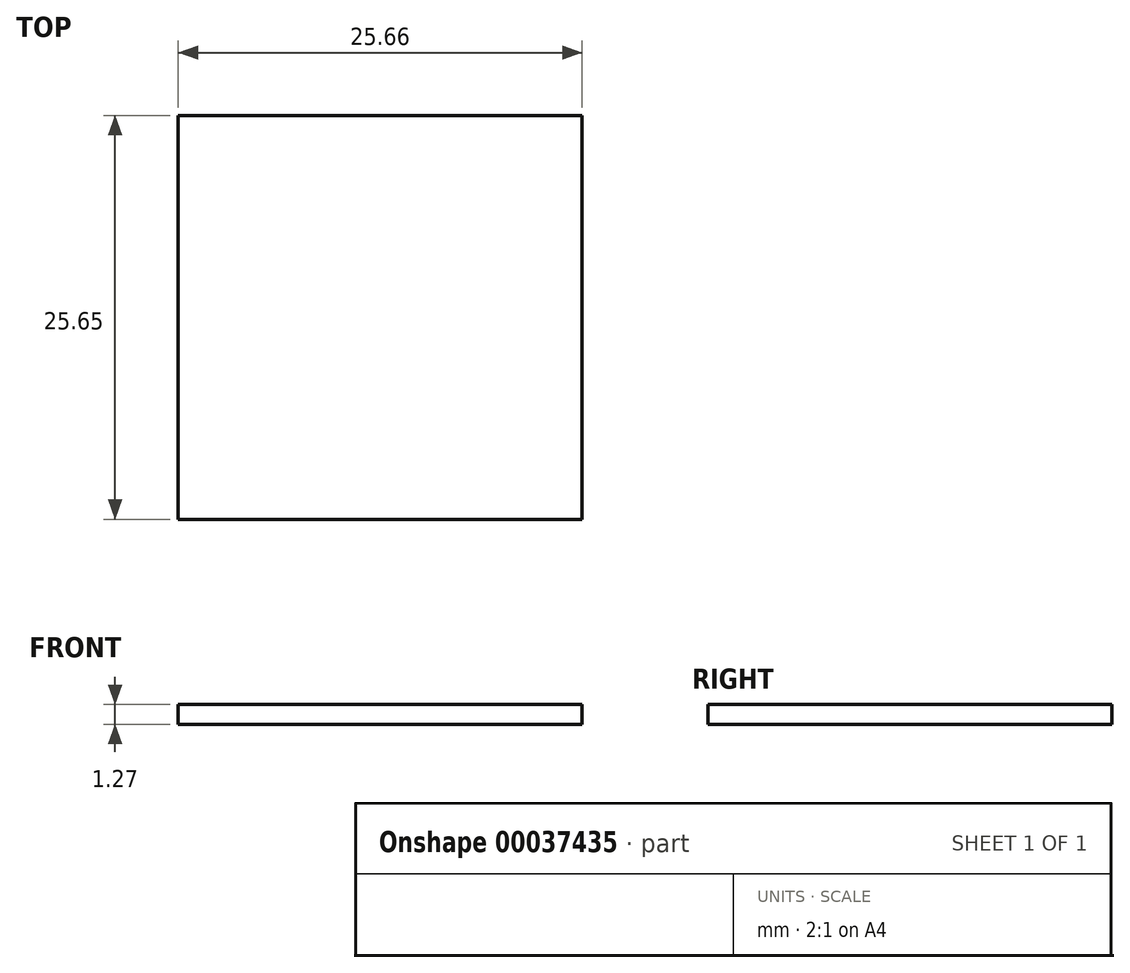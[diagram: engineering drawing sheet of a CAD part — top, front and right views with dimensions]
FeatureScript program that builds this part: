
annotation { "Feature Type Name" : "Feature", "Feature Type Description" : "" }
export const myFeature = defineFeature(function(context is Context, id is Id, definition is map)
    precondition{}
    {
        {
            var Q0;
            Q0=qCreatedBy(makeId("Top.planeOp"),FACE);
            var sketch = newSketch(context, id + "F0", { "sketchPlane" : qUnion([Q0])});
            skLineSegment(sketch, "E0.rect.bottom", {"start": v(9.03, -14.2) * mm, "end": v(-51, -14.2) * mm});
            skLineSegment(sketch, "E0.rect.top", {"start": v(9.03, 56.87) * mm, "end": v(-51, 56.87) * mm});
            skLineSegment(sketch, "E0.rect.left", {"start": v(9.03, -14.2) * mm, "end": v(9.03, 56.87) * mm});
            skLineSegment(sketch, "E0.rect.right", {"start": v(-51, -14.2) * mm, "end": v(-51, 56.87) * mm});
            skPoint(sketch, "E0.rect.middle", {"position": v(-21, 21.34) * mm});
            skSolve(sketch);
        }
        {
            var Q0;
            Q0=makeQuery(id+"F0.imprint","IMPRINT",FACE,{"disambiguationData":[TD([[makeQuery(id+"F0.imprint","IMPRINT",EDGE,{"derivedFrom":sQuery(id+"F0.wireOp",EDGE,"E0.rect.bottom")}),-1.0]])]});
            extrude(context, id + "F1", {"entities" : qUnion([Q0]), "depth" : 1.27 * mm});
        }
        {
            var Q0;
            Q0=makeQuery(id+"F1.opExtrude","SWEPT_FACE",FACE,{"disambiguationData":[OSD([sQuery(id+"F0.wireOp",EDGE,"E0.rect.bottom")])]});
            extrude(context, id + "F2", {"entities" : qUnion([Q0]), "operationType" : NewBodyOperationType.REMOVE, "oppositeDirection" : true, "depth" : 45.42 * mm});
        }
        {
            var Q0;
            Q0=makeQuery(id+"F1.opExtrude","SWEPT_FACE",FACE,{"disambiguationData":[OSD([sQuery(id+"F0.wireOp",EDGE,"E0.rect.left")])]});
            extrude(context, id + "F3", {"entities" : qUnion([Q0]), "operationType" : NewBodyOperationType.REMOVE, "oppositeDirection" : true, "depth" : 34.38 * mm});
        }
    });
